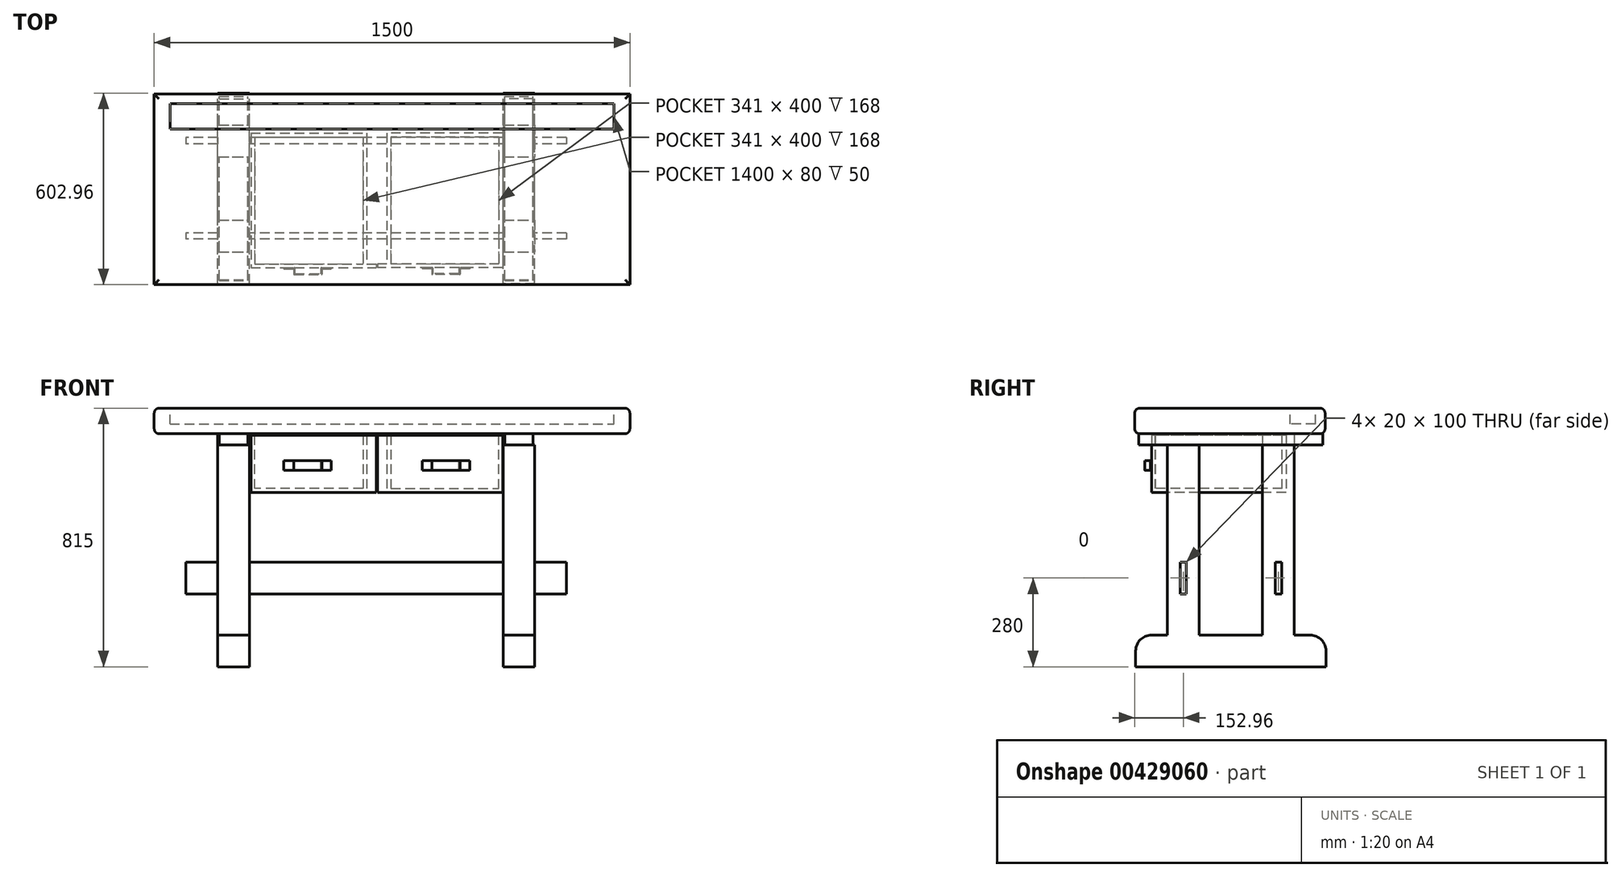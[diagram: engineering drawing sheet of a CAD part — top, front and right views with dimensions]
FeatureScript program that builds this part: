
annotation { "Feature Type Name" : "Feature", "Feature Type Description" : "" }
export const myFeature = defineFeature(function(context is Context, id is Id, definition is map)
    precondition{}
    {
        {
            var Q0;
            Q0=qCreatedBy(makeId("Top.planeOp"),FACE);
            var sketch = newSketch(context, id + "F0", { "sketchPlane" : qUnion([Q0])});
            skLineSegment(sketch, "E0.bottom", {"start": v(0, 0) * mm, "end": v(100, 0) * mm});
            skLineSegment(sketch, "E0.top", {"start": v(0, 600) * mm, "end": v(100, 600) * mm});
            skLineSegment(sketch, "E0.left", {"start": v(0, 0) * mm, "end": v(0, 600) * mm});
            skLineSegment(sketch, "E0.right", {"start": v(100, 0) * mm, "end": v(100, 600) * mm});
            skLineSegment(sketch, "E1.bottom", {"start": v(1000, 0) * mm, "end": v(900, 0) * mm});
            skLineSegment(sketch, "E1.top", {"start": v(1000, 600) * mm, "end": v(900, 600) * mm});
            skLineSegment(sketch, "E1.left", {"start": v(1000, 0) * mm, "end": v(1000, 600) * mm});
            skLineSegment(sketch, "E1.right", {"start": v(900, 0) * mm, "end": v(900, 600) * mm});
            skSolve(sketch);
        }
        {
            var Q0;
            Q0=makeQuery(id+"F0.imprint","IMPRINT",FACE,{"disambiguationData":[TD([[makeQuery(id+"F0.imprint","IMPRINT",EDGE,{"derivedFrom":sQuery(id+"F0.wireOp",EDGE,"E0.bottom")}),1.0]])]});
            var Q1;
            Q1=makeQuery(id+"F0.imprint","IMPRINT",FACE,{"disambiguationData":[TD([[makeQuery(id+"F0.imprint","IMPRINT",EDGE,{"derivedFrom":sQuery(id+"F0.wireOp",EDGE,"E1.bottom")}),-1.0]])]});
            extrude(context, id + "F1", {"entities" : qUnion([Q0, Q1]), "depth" : 100 * mm});
        }
        {
            var Q0;
            Q0=makeQuery(id+"F1.opExtrude","CAP_FACE",FACE,{"disambiguationData":[OSD([sQuery(id+"F0.wireOp",EDGE,"E0.bottom"),sQuery(id+"F0.wireOp",EDGE,"E0.top"),sQuery(id+"F0.wireOp",EDGE,"E0.left"),sQuery(id+"F0.wireOp",EDGE,"E0.right")])],"isStart":false});
            var sketch = newSketch(context, id + "F2", { "sketchPlane" : qUnion([Q0])});
            skLineSegment(sketch, "E2.bottom", {"start": v(0, 500) * mm, "end": v(100, 500) * mm});
            skLineSegment(sketch, "E2.top", {"start": v(0, 400) * mm, "end": v(100, 400) * mm});
            skLineSegment(sketch, "E2.left", {"start": v(0, 500) * mm, "end": v(0, 400) * mm});
            skLineSegment(sketch, "E2.right", {"start": v(100, 500) * mm, "end": v(100, 400) * mm});
            skLineSegment(sketch, "E3.bottom", {"start": v(0, 200) * mm, "end": v(100, 200) * mm});
            skLineSegment(sketch, "E3.top", {"start": v(0, 100) * mm, "end": v(100, 100) * mm});
            skLineSegment(sketch, "E3.left", {"start": v(0, 200) * mm, "end": v(0, 100) * mm});
            skLineSegment(sketch, "E3.right", {"start": v(100, 200) * mm, "end": v(100, 100) * mm});
            skLineSegment(sketch, "E4.1.0.0", {"start": v(900, 200) * mm, "end": v(900, 100) * mm});
            skLineSegment(sketch, "E4.1.0.1", {"start": v(1000, 200) * mm, "end": v(1000, 100) * mm});
            skLineSegment(sketch, "E4.1.0.2", {"start": v(900, 100) * mm, "end": v(1000, 100) * mm});
            skLineSegment(sketch, "E4.1.0.3", {"start": v(900, 200) * mm, "end": v(1000, 200) * mm});
            skLineSegment(sketch, "E4.1.0.4", {"start": v(1000, 500) * mm, "end": v(1000, 400) * mm});
            skLineSegment(sketch, "E4.1.0.5", {"start": v(900, 500) * mm, "end": v(900, 400) * mm});
            skLineSegment(sketch, "E4.1.0.6", {"start": v(900, 400) * mm, "end": v(1000, 400) * mm});
            skLineSegment(sketch, "E4.1.0.7", {"start": v(900, 500) * mm, "end": v(1000, 500) * mm});
            skLineSegment(sketch, "E4.direction1", {"start": v(0, 100) * mm, "end": v(900, 100) * mm, "construction": true});
            skSolve(sketch);
        }
        {
            var Q0;
            Q0=makeQuery(id+"F2.imprint","IMPRINT",FACE,{"disambiguationData":[TD([[makeQuery(id+"F2.imprint","IMPRINT",EDGE,{"derivedFrom":sQuery(id+"F2.wireOp",EDGE,"E2.bottom")}),-1.0]])]});
            var Q1;
            Q1=makeQuery(id+"F2.imprint","IMPRINT",FACE,{"disambiguationData":[TD([[makeQuery(id+"F2.imprint","IMPRINT",EDGE,{"derivedFrom":sQuery(id+"F2.wireOp",EDGE,"E4.1.0.4")}),-1.0]])]});
            var Q2;
            Q2=makeQuery(id+"F2.imprint","IMPRINT",FACE,{"disambiguationData":[TD([[makeQuery(id+"F2.imprint","IMPRINT",EDGE,{"derivedFrom":sQuery(id+"F2.wireOp",EDGE,"E4.1.0.0")}),1.0]])]});
            var Q3;
            Q3=makeQuery(id+"F2.imprint","IMPRINT",FACE,{"disambiguationData":[TD([[makeQuery(id+"F2.imprint","IMPRINT",EDGE,{"derivedFrom":sQuery(id+"F2.wireOp",EDGE,"E3.bottom")}),-1.0]])]});
            extrude(context, id + "F3", {"entities" : qUnion([Q0, Q1, Q2, Q3]), "depth" : 600 * mm});
        }
        {
            var Q0;
            Q0=qCreatedBy(makeId("Right.planeOp"),FACE);
            cPlane(context, id + "F4", {"entities" : qUnion([Q0]), "cplaneType" : CPlaneType.OFFSET, "offset" : 100 * mm, "oppositeDirection" : true, "width" : 150 * mm, "height" : 150 * mm});
        }
        {
            var Q0;
            Q0=qCreatedBy(id+"F4.planeOp",FACE);
            var sketch = newSketch(context, id + "F5", { "sketchPlane" : qUnion([Q0])});
            skLineSegment(sketch, "E5.bottom", {"start": v(160, 330) * mm, "end": v(140, 330) * mm});
            skLineSegment(sketch, "E5.top", {"start": v(160, 230) * mm, "end": v(140, 230) * mm});
            skLineSegment(sketch, "E5.left", {"start": v(160, 330) * mm, "end": v(160, 230) * mm});
            skLineSegment(sketch, "E5.right", {"start": v(140, 330) * mm, "end": v(140, 230) * mm});
            skLineSegment(sketch, "E6.1.0.0", {"start": v(460, 330) * mm, "end": v(440, 330) * mm});
            skLineSegment(sketch, "E6.1.0.1", {"start": v(460, 230) * mm, "end": v(440, 230) * mm});
            skLineSegment(sketch, "E6.1.0.2", {"start": v(460, 330) * mm, "end": v(460, 230) * mm});
            skLineSegment(sketch, "E6.1.0.3", {"start": v(440, 330) * mm, "end": v(440, 230) * mm});
            skLineSegment(sketch, "E6.direction1", {"start": v(140, 230) * mm, "end": v(440, 230) * mm, "construction": true});
            skSolve(sketch);
        }
        {
            var Q0;
            Q0=makeQuery(id+"F5.imprint","IMPRINT",FACE,{"disambiguationData":[TD([[makeQuery(id+"F5.imprint","IMPRINT",EDGE,{"derivedFrom":sQuery(id+"F5.wireOp",EDGE,"E6.1.0.0")}),1.0]])]});
            var Q1;
            Q1=makeQuery(id+"F5.imprint","IMPRINT",FACE,{"disambiguationData":[TD([[makeQuery(id+"F5.imprint","IMPRINT",EDGE,{"derivedFrom":sQuery(id+"F5.wireOp",EDGE,"E5.bottom")}),1.0]])]});
            extrude(context, id + "F6", {"entities" : qUnion([Q0, Q1]), "depth" : 1200 * mm});
        }
        {
            var Q0;
            Q0=makeQuery(id+"F1.opExtrude","CAP_EDGE",EDGE,{"disambiguationData":[OSD([sQuery(id+"F0.wireOp",EDGE,"E0.top")])],"isStart":false});
            var Q1;
            Q1=makeQuery(id+"F1.opExtrude","CAP_EDGE",EDGE,{"disambiguationData":[OSD([sQuery(id+"F0.wireOp",EDGE,"E0.bottom")])],"isStart":false});
            var Q2;
            Q2=makeQuery(id+"F1.opExtrude","CAP_EDGE",EDGE,{"disambiguationData":[OSD([sQuery(id+"F0.wireOp",EDGE,"E1.bottom")])],"isStart":false});
            var Q3;
            Q3=makeQuery(id+"F1.opExtrude","CAP_EDGE",EDGE,{"disambiguationData":[OSD([sQuery(id+"F0.wireOp",EDGE,"E1.top")])],"isStart":false});
            fillet(context, id + "F7", {"entities" : qUnion([Q0, Q1, Q2, Q3]), "radius" : 50 * mm, "tangentPropagation" : true, "allowEdgeOverflow" : false});
        }
        {
            var Q0;
            Q0=makeQuery(id+"F3.opExtrude","CAP_FACE",FACE,{"disambiguationData":[OSD([sQuery(id+"F2.wireOp",EDGE,"E2.bottom"),sQuery(id+"F2.wireOp",EDGE,"E2.top"),sQuery(id+"F2.wireOp",EDGE,"E2.left"),sQuery(id+"F2.wireOp",EDGE,"E2.right")])],"isStart":false});
            var sketch = newSketch(context, id + "F8", { "sketchPlane" : qUnion([Q0])});
            skLineSegment(sketch, "E7.bottom", {"start": v(5, 10) * mm, "end": v(95, 10) * mm});
            skLineSegment(sketch, "E7.top", {"start": v(5, 590) * mm, "end": v(95, 590) * mm});
            skLineSegment(sketch, "E7.left", {"start": v(5, 10) * mm, "end": v(5, 590) * mm});
            skLineSegment(sketch, "E7.right", {"start": v(95, 10) * mm, "end": v(95, 590) * mm});
            skLineSegment(sketch, "E8.1.0.0", {"start": v(995, 10) * mm, "end": v(995, 590) * mm});
            skLineSegment(sketch, "E8.1.0.1", {"start": v(905, 10) * mm, "end": v(905, 590) * mm});
            skLineSegment(sketch, "E8.1.0.2", {"start": v(905, 590) * mm, "end": v(995, 590) * mm});
            skLineSegment(sketch, "E8.1.0.3", {"start": v(905, 10) * mm, "end": v(995, 10) * mm});
            skSolve(sketch);
        }
        {
            var Q0;
            Q0=makeQuery(id+"F8.imprint","IMPRINT",FACE,{"disambiguationData":[TD([[makeQuery(id+"F8.imprint","IMPRINT",EDGE,{"derivedFrom":sQuery(id+"F8.wireOp",EDGE,"E8.1.0.0")}),1.0]])]});
            var Q1;
            {var subQ0=sQuery(id+"F8.wireOp",EDGE,"E7.top");Q1=makeQuery(id+"F8.imprint","IMPRINT",FACE,{"disambiguationData":[TD([[makeQuery(id+"F8.imprint","IMPRINT",EDGE,{"derivedFrom":subQ0}),-1.0]])]});}
            var Q2;
            {var subQ1=makeQuery(id+"F3.opExtrude","CAP_EDGE",EDGE,{"disambiguationData":[OSD([sQuery(id+"F2.wireOp",EDGE,"E2.bottom")])],"isStart":false});Q2=makeQuery(id+"F8.imprint","IMPRINT",FACE,{"disambiguationData":[TD([[makeQuery(id+"F8.imprint","IMPRINT",EDGE,{"derivedFrom":subQ1}),-1.0]])]});}
            var Q3;
            {var subQ0=sQuery(id+"F8.wireOp",EDGE,"E7.bottom");Q3=makeQuery(id+"F8.imprint","IMPRINT",FACE,{"disambiguationData":[TD([[makeQuery(id+"F8.imprint","IMPRINT",EDGE,{"derivedFrom":subQ0}),1.0]])]});}
            extrude(context, id + "F9", {"entities" : qUnion([Q0, Q1, Q2, Q3]), "depth" : 35 * mm});
        }
        {
            var Q0;
            Q0=makeQuery(id+"F9.opExtrude","CAP_FACE",FACE,{"disambiguationData":[OSD([sQuery(id+"F8.wireOp",EDGE,"E8.1.0.0"),sQuery(id+"F8.wireOp",EDGE,"E8.1.0.1"),sQuery(id+"F8.wireOp",EDGE,"E8.1.0.2"),sQuery(id+"F8.wireOp",EDGE,"E8.1.0.3")])],"isStart":false});
            var sketch = newSketch(context, id + "F10", { "sketchPlane" : qUnion([Q0])});
            skLineSegment(sketch, "E9.bottom", {"start": v(-200, 597.04) * mm, "end": v(1300, 597.04) * mm});
            skLineSegment(sketch, "E9.top", {"start": v(-200, -2.96) * mm, "end": v(1300, -2.96) * mm});
            skLineSegment(sketch, "E9.left", {"start": v(-200, 597.04) * mm, "end": v(-200, -2.96) * mm});
            skLineSegment(sketch, "E9.right", {"start": v(1300, 597.04) * mm, "end": v(1300, -2.96) * mm});
            skSolve(sketch);
        }
        {
            var Q0;
            Q0=makeQuery(id+"F10.imprint","IMPRINT",FACE,{"disambiguationData":[TD([[makeQuery(id+"F10.imprint","IMPRINT",EDGE,{"derivedFrom":sQuery(id+"F10.wireOp",EDGE,"E9.top")}),1.0]])]});
            var Q1;
            {var subQ5=makeQuery(id+"F9.opExtrude","CAP_EDGE",EDGE,{"disambiguationData":[OSD([sQuery(id+"F8.wireOp",EDGE,"E8.1.0.3")])],"isStart":false});Q1=makeQuery(id+"F10.imprint","IMPRINT",FACE,{"disambiguationData":[TD([[makeQuery(id+"F10.imprint","IMPRINT",EDGE,{"derivedFrom":subQ5}),1.0]])]});}
            extrude(context, id + "F11", {"entities" : qUnion([Q0, Q1]), "depth" : 80 * mm});
        }
        {
            var Q0;
            Q0=makeQuery(id+"F11.opExtrude","CAP_FACE",FACE,{"disambiguationData":[OSD([sQuery(id+"F10.wireOp",EDGE,"E9.bottom"),sQuery(id+"F10.wireOp",EDGE,"E9.top"),sQuery(id+"F10.wireOp",EDGE,"E9.left"),sQuery(id+"F10.wireOp",EDGE,"E9.right")])],"isStart":false});
            var Q1;
            Q1=makeQuery(id+"F11.opExtrude","CAP_FACE",FACE,{"disambiguationData":[OSD([sQuery(id+"F10.wireOp",EDGE,"E9.bottom"),sQuery(id+"F10.wireOp",EDGE,"E9.top"),sQuery(id+"F10.wireOp",EDGE,"E9.left"),sQuery(id+"F10.wireOp",EDGE,"E9.right")])],"isStart":true});
            fillet(context, id + "F12", {"entities" : qUnion([Q0, Q1]), "radius" : 15 * mm, "tangentPropagation" : true, "allowEdgeOverflow" : false});
        }
        {
            var Q0;
            Q0=makeQuery(id+"F1.opExtrude","SWEPT_BODY",BODY,{"disambiguationData":[OSD([sQuery(id+"F0.wireOp",EDGE,"E0.bottom"),sQuery(id+"F0.wireOp",EDGE,"E0.top"),sQuery(id+"F0.wireOp",EDGE,"E0.left"),sQuery(id+"F0.wireOp",EDGE,"E0.right")])]});
            var Q1;
            Q1=makeQuery(id+"F1.opExtrude","SWEPT_BODY",BODY,{"disambiguationData":[OSD([sQuery(id+"F0.wireOp",EDGE,"E1.bottom"),sQuery(id+"F0.wireOp",EDGE,"E1.top"),sQuery(id+"F0.wireOp",EDGE,"E1.left"),sQuery(id+"F0.wireOp",EDGE,"E1.right")])]});
            var Q2;
            Q2=makeQuery(id+"F3.opExtrude","SWEPT_BODY",BODY,{"disambiguationData":[OSD([sQuery(id+"F2.wireOp",EDGE,"E2.bottom"),sQuery(id+"F2.wireOp",EDGE,"E2.top"),sQuery(id+"F2.wireOp",EDGE,"E2.left"),sQuery(id+"F2.wireOp",EDGE,"E2.right")])]});
            var Q3;
            Q3=makeQuery(id+"F3.opExtrude","SWEPT_BODY",BODY,{"disambiguationData":[OSD([sQuery(id+"F2.wireOp",EDGE,"E3.bottom"),sQuery(id+"F2.wireOp",EDGE,"E3.top"),sQuery(id+"F2.wireOp",EDGE,"E3.left"),sQuery(id+"F2.wireOp",EDGE,"E3.right")])]});
            var Q4;
            Q4=makeQuery(id+"F3.opExtrude","SWEPT_BODY",BODY,{"disambiguationData":[OSD([sQuery(id+"F2.wireOp",EDGE,"E4.1.0.0"),sQuery(id+"F2.wireOp",EDGE,"E4.1.0.1"),sQuery(id+"F2.wireOp",EDGE,"E4.1.0.2"),sQuery(id+"F2.wireOp",EDGE,"E4.1.0.3")])]});
            var Q5;
            Q5=makeQuery(id+"F3.opExtrude","SWEPT_BODY",BODY,{"disambiguationData":[OSD([sQuery(id+"F2.wireOp",EDGE,"E4.1.0.4"),sQuery(id+"F2.wireOp",EDGE,"E4.1.0.5"),sQuery(id+"F2.wireOp",EDGE,"E4.1.0.6"),sQuery(id+"F2.wireOp",EDGE,"E4.1.0.7")])]});
            var Q6;
            Q6=makeQuery(id+"F6.opExtrude","SWEPT_BODY",BODY,{"disambiguationData":[OSD([sQuery(id+"F5.wireOp",EDGE,"E5.bottom"),sQuery(id+"F5.wireOp",EDGE,"E5.top"),sQuery(id+"F5.wireOp",EDGE,"E5.left"),sQuery(id+"F5.wireOp",EDGE,"E5.right")])]});
            var Q7;
            Q7=makeQuery(id+"F6.opExtrude","SWEPT_BODY",BODY,{"disambiguationData":[OSD([sQuery(id+"F5.wireOp",EDGE,"E6.1.0.0"),sQuery(id+"F5.wireOp",EDGE,"E6.1.0.1"),sQuery(id+"F5.wireOp",EDGE,"E6.1.0.2"),sQuery(id+"F5.wireOp",EDGE,"E6.1.0.3")])]});
            var Q8;
            Q8=makeQuery(id+"F9.opExtrude","SWEPT_BODY",BODY,{"disambiguationData":[OSD([sQuery(id+"F8.wireOp",EDGE,"E7.bottom"),sQuery(id+"F8.wireOp",EDGE,"E7.top"),sQuery(id+"F8.wireOp",EDGE,"E7.left"),sQuery(id+"F8.wireOp",EDGE,"E7.right")])]});
            var Q9;
            Q9=makeQuery(id+"F9.opExtrude","SWEPT_BODY",BODY,{"disambiguationData":[OSD([sQuery(id+"F8.wireOp",EDGE,"E8.1.0.0"),sQuery(id+"F8.wireOp",EDGE,"E8.1.0.1"),sQuery(id+"F8.wireOp",EDGE,"E8.1.0.2"),sQuery(id+"F8.wireOp",EDGE,"E8.1.0.3")])]});
            var Q10;
            Q10=makeQuery(id+"F11.opExtrude","SWEPT_BODY",BODY,{"disambiguationData":[OSD([sQuery(id+"F10.wireOp",EDGE,"E9.bottom"),sQuery(id+"F10.wireOp",EDGE,"E9.top"),sQuery(id+"F10.wireOp",EDGE,"E9.left"),sQuery(id+"F10.wireOp",EDGE,"E9.right")])]});
            booleanBodies(context, id + "F13", {"operationType" : BooleanOperationType.UNION, "tools" : qUnion([Q0, Q1, Q2, Q3, Q4, Q5, Q6, Q7, Q8, Q9, Q10])});
        }
        {
            var Q0;
            Q0=makeQuery(id+"F11.opExtrude","CAP_FACE",FACE,{"disambiguationData":[OSD([sQuery(id+"F10.wireOp",EDGE,"E9.bottom"),sQuery(id+"F10.wireOp",EDGE,"E9.top"),sQuery(id+"F10.wireOp",EDGE,"E9.left"),sQuery(id+"F10.wireOp",EDGE,"E9.right")])],"isStart":false});
            var sketch = newSketch(context, id + "F14", { "sketchPlane" : qUnion([Q0])});
            skLineSegment(sketch, "E10.bottom", {"start": v(-150, 567.04) * mm, "end": v(1250, 567.04) * mm});
            skLineSegment(sketch, "E10.top", {"start": v(-150, 487.04) * mm, "end": v(1250, 487.04) * mm});
            skLineSegment(sketch, "E10.left", {"start": v(-150, 567.04) * mm, "end": v(-150, 487.04) * mm});
            skLineSegment(sketch, "E10.right", {"start": v(1250, 567.04) * mm, "end": v(1250, 487.04) * mm});
            skSolve(sketch);
        }
        {
            var Q0;
            Q0=makeQuery(id+"F14.imprint","IMPRINT",FACE,{"disambiguationData":[TD([[makeQuery(id+"F14.imprint","IMPRINT",EDGE,{"derivedFrom":sQuery(id+"F14.wireOp",EDGE,"E10.bottom")}),-1.0]])]});
            extrude(context, id + "F15", {"entities" : qUnion([Q0]), "operationType" : NewBodyOperationType.REMOVE, "oppositeDirection" : true, "depth" : 50 * mm});
        }
        {
            var Q0;
            Q0=qCreatedBy(makeId("Front.planeOp"),FACE);
            cPlane(context, id + "F16", {"entities" : qUnion([Q0]), "cplaneType" : CPlaneType.OFFSET, "offset" : 50 * mm, "oppositeDirection" : true, "width" : 150 * mm, "height" : 150 * mm});
        }
        {
            var Q0;
            Q0=qCreatedBy(id+"F16.planeOp",FACE);
            var sketch = newSketch(context, id + "F17", { "sketchPlane" : qUnion([Q0])});
            skLineSegment(sketch, "E11.bottom", {"start": v(105, 730) * mm, "end": v(500, 730) * mm});
            skLineSegment(sketch, "E11.top", {"start": v(105, 550) * mm, "end": v(500, 550) * mm});
            skLineSegment(sketch, "E11.left", {"start": v(105, 730) * mm, "end": v(105, 550) * mm});
            skLineSegment(sketch, "E11.right", {"start": v(500, 730) * mm, "end": v(500, 550) * mm});
            skLineSegment(sketch, "E12", {"start": v(105, 730) * mm, "end": v(900, 730) * mm, "construction": true});
            skPoint(sketch, "E12.startSnap0", {"position": v(105, 640) * mm});
            skLineSegment(sketch, "E13", {"start": v(502.5, 730) * mm, "end": v(502.5, 502.03) * mm, "construction": true});
            skSolve(sketch);
        }
        {
            var Q0;
            Q0=makeQuery(id+"F17.imprint","IMPRINT",FACE,{"disambiguationData":[TD([[makeQuery(id+"F17.imprint","IMPRINT",EDGE,{"derivedFrom":sQuery(id+"F17.wireOp",EDGE,"E11.bottom")}),-1.0]])]});
            extrude(context, id + "F18", {"entities" : qUnion([Q0]), "oppositeDirection" : true, "depth" : 12 * mm});
        }
        {
            var Q0;
            Q0=makeQuery(id+"F18.opExtrude","CAP_FACE",FACE,{"disambiguationData":[OSD([sQuery(id+"F17.wireOp",EDGE,"E11.bottom"),sQuery(id+"F17.wireOp",EDGE,"E11.top"),sQuery(id+"F17.wireOp",EDGE,"E11.left"),sQuery(id+"F17.wireOp",EDGE,"E11.right")])],"isStart":false});
            var sketch = newSketch(context, id + "F19", { "sketchPlane" : qUnion([Q0])});
            skLineSegment(sketch, "E14.bottom", {"start": v(-470, 730) * mm, "end": v(-458, 730) * mm});
            skLineSegment(sketch, "E14.top", {"start": v(-470, 550) * mm, "end": v(-458, 550) * mm});
            skLineSegment(sketch, "E14.left", {"start": v(-470, 730) * mm, "end": v(-470, 550) * mm});
            skLineSegment(sketch, "E14.right", {"start": v(-458, 730) * mm, "end": v(-458, 562) * mm});
            skLineSegment(sketch, "E15.bottom", {"start": v(-470, 550) * mm, "end": v(-105, 550) * mm});
            skLineSegment(sketch, "E15.top", {"start": v(-458, 562) * mm, "end": v(-117, 562) * mm});
            skLineSegment(sketch, "E15.left", {"start": v(-470, 550) * mm, "end": v(-470, 562) * mm});
            skLineSegment(sketch, "E15.right", {"start": v(-105, 550) * mm, "end": v(-105, 562) * mm});
            skLineSegment(sketch, "E16.bottom", {"start": v(-105, 550) * mm, "end": v(-117, 550) * mm});
            skLineSegment(sketch, "E16.top", {"start": v(-105, 730) * mm, "end": v(-117, 730) * mm});
            skLineSegment(sketch, "E16.left", {"start": v(-105, 550) * mm, "end": v(-105, 730) * mm});
            skLineSegment(sketch, "E16.right", {"start": v(-117, 562) * mm, "end": v(-117, 730) * mm});
            skLineSegment(sketch, "E17", {"start": v(-287.5, 562) * mm, "end": v(-287.5, 550) * mm, "construction": true});
            skSolve(sketch);
        }
        {
            var Q0;
            Q0=makeQuery(id+"F19.imprint","IMPRINT",FACE,{"disambiguationData":[TD([[makeQuery(id+"F19.imprint","IMPRINT",EDGE,{"derivedFrom":sQuery(id+"F19.wireOp",EDGE,"E14.bottom")}),1.0]])]});
            extrude(context, id + "F20", {"entities" : qUnion([Q0]), "operationType" : NewBodyOperationType.ADD, "depth" : 400 * mm});
        }
        {
            var Q0;
            Q0=makeQuery(id+"F20.opExtrude","CAP_FACE",FACE,{"disambiguationData":[OSD([sQuery(id+"F19.wireOp",EDGE,"E14.bottom"),sQuery(id+"F19.wireOp",EDGE,"E14.left"),sQuery(id+"F19.wireOp",EDGE,"E14.right"),sQuery(id+"F19.wireOp",EDGE,"E15.bottom"),sQuery(id+"F19.wireOp",EDGE,"E15.top"),sQuery(id+"F19.wireOp",EDGE,"E15.left"),sQuery(id+"F19.wireOp",EDGE,"E16.bottom"),sQuery(id+"F19.wireOp",EDGE,"E16.top"),sQuery(id+"F19.wireOp",EDGE,"E16.left"),sQuery(id+"F19.wireOp",EDGE,"E16.right")])],"isStart":false});
            var sketch = newSketch(context, id + "F21", { "sketchPlane" : qUnion([Q0])});
            skLineSegment(sketch, "E18.bottom", {"start": v(-470, 730) * mm, "end": v(-105, 730) * mm});
            skLineSegment(sketch, "E18.top", {"start": v(-470, 550) * mm, "end": v(-105, 550) * mm});
            skLineSegment(sketch, "E18.left", {"start": v(-470, 730) * mm, "end": v(-470, 550) * mm});
            skLineSegment(sketch, "E18.right", {"start": v(-105, 730) * mm, "end": v(-105, 550) * mm});
            skSolve(sketch);
        }
        {
            var Q0;
            Q0=makeQuery(id+"F21.imprint","IMPRINT",FACE,{"disambiguationData":[TD([[makeQuery(id+"F21.imprint","IMPRINT",EDGE,{"derivedFrom":sQuery(id+"F21.wireOp",EDGE,"E18.top")}),-1.0]])]});
            var Q1;
            {var subQ1=makeQuery(id+"F20.opExtrude","CAP_EDGE",EDGE,{"disambiguationData":[OSD([sQuery(id+"F19.wireOp",EDGE,"E14.right")])],"isStart":false});Q1=makeQuery(id+"F21.imprint","IMPRINT",FACE,{"disambiguationData":[TD([[makeQuery(id+"F21.imprint","IMPRINT",EDGE,{"derivedFrom":subQ1}),1.0]])]});}
            extrude(context, id + "F22", {"entities" : qUnion([Q0, Q1]), "operationType" : NewBodyOperationType.ADD, "depth" : 12 * mm});
        }
        {
            var Q0;
            Q0=qCreatedBy(makeId("Top.planeOp"),FACE);
            cPlane(context, id + "F23", {"entities" : qUnion([Q0]), "cplaneType" : CPlaneType.OFFSET, "offset" : 650 * mm, "width" : 150 * mm, "height" : 150 * mm});
        }
        {
            var Q0;
            Q0=qCreatedBy(id+"F23.planeOp",FACE);
            var sketch = newSketch(context, id + "F24", { "sketchPlane" : qUnion([Q0])});
            skLineSegment(sketch, "E19.bottom", {"start": v(208.7, 50) * mm, "end": v(241.2, 50) * mm});
            skLineSegment(sketch, "E19.top", {"start": v(208.7, 47) * mm, "end": v(238.7, 47) * mm});
            skLineSegment(sketch, "E19.left", {"start": v(208.7, 50) * mm, "end": v(208.7, 47) * mm});
            skLineSegment(sketch, "E19.right", {"start": v(358.7, 50) * mm, "end": v(358.7, 47) * mm});
            skLineSegment(sketch, "E20.top", {"start": v(241.2, 28.45) * mm, "end": v(242.7, 28.45) * mm});
            skLineSegment(sketch, "E20.left", {"start": v(239.7, 46) * mm, "end": v(239.7, 29.95) * mm});
            skLineSegment(sketch, "E20.right", {"start": v(242.7, 48.5) * mm, "end": v(242.7, 32.45) * mm});
            skLineSegment(sketch, "E21.bottom", {"start": v(327.2, 50) * mm, "end": v(328.2, 50) * mm});
            skLineSegment(sketch, "E21.top", {"start": v(325.7, 28.45) * mm, "end": v(327.2, 28.45) * mm});
            skLineSegment(sketch, "E21.left", {"start": v(325.7, 48.5) * mm, "end": v(325.7, 32.45) * mm});
            skLineSegment(sketch, "E21.right", {"start": v(328.7, 47) * mm, "end": v(328.7, 29.95) * mm});
            skLineSegment(sketch, "E22", {"start": v(242.7, 28.45) * mm, "end": v(325.7, 28.45) * mm});
            skLineSegment(sketch, "E23", {"start": v(243.7, 31.45) * mm, "end": v(324.7, 31.45) * mm});
            skLineSegment(sketch, "E24.trimOffspring", {"start": v(325.7, 50) * mm, "end": v(358.7, 50) * mm});
            skLineSegment(sketch, "E25.trimOffspring", {"start": v(328.7, 47) * mm, "end": v(358.7, 47) * mm});
            skPoint(sketch, "E26.visualSharp", {"position": v(239.7, 47) * mm});
            skArc(sketch, "E26.filletArc", {"start": v(239.7, 46) * mm, "mid": v(239.41, 46.7) * mm, "end": v(238.7, 47) * mm});
            skPoint(sketch, "E27.visualSharp", {"position": v(239.7, 28.45) * mm});
            skArc(sketch, "E27.filletArc", {"start": v(239.7, 29.95) * mm, "mid": v(240.14, 28.9) * mm, "end": v(241.2, 28.45) * mm});
            skPoint(sketch, "E28.visualSharp", {"position": v(242.7, 31.45) * mm});
            skArc(sketch, "E28.filletArc", {"start": v(242.7, 32.45) * mm, "mid": v(243, 31.74) * mm, "end": v(243.7, 31.45) * mm});
            skPoint(sketch, "E29.visualSharp", {"position": v(325.7, 31.45) * mm});
            skArc(sketch, "E29.filletArc", {"start": v(324.7, 31.45) * mm, "mid": v(325.41, 31.74) * mm, "end": v(325.7, 32.45) * mm});
            skPoint(sketch, "E30.visualSharp", {"position": v(328.7, 28.45) * mm});
            skArc(sketch, "E30.filletArc", {"start": v(327.2, 28.45) * mm, "mid": v(328.26, 28.9) * mm, "end": v(328.7, 29.95) * mm});
            skPoint(sketch, "E31.visualSharp", {"position": v(242.7, 50) * mm});
            skArc(sketch, "E31.filletArc", {"start": v(242.7, 48.5) * mm, "mid": v(242.26, 49.56) * mm, "end": v(241.2, 50) * mm});
            skPoint(sketch, "E32.visualSharp", {"position": v(325.7, 50) * mm});
            skArc(sketch, "E32.filletArc", {"start": v(327.2, 50) * mm, "mid": v(326.14, 49.56) * mm, "end": v(325.7, 48.5) * mm});
            skLineSegment(sketch, "E33", {"start": v(105, 50) * mm, "end": v(500, 50) * mm});
            skLineSegment(sketch, "E34", {"start": v(284.2, 31.45) * mm, "end": v(284.2, 50) * mm, "construction": true});
            skPoint(sketch, "E34.endSnap0", {"position": v(224.95, 50) * mm});
            skSolve(sketch);
        }
        {
            var Q0;
            Q0=makeQuery(id+"F24.imprint","IMPRINT",FACE,{"disambiguationData":[TD([[makeQuery(id+"F24.imprint","IMPRINT",EDGE,{"derivedFrom":sQuery(id+"F24.wireOp",EDGE,"E19.top")}),1.0]])]});
            extrude(context, id + "F25", {"entities" : qUnion([Q0]), "operationType" : NewBodyOperationType.ADD, "oppositeDirection" : true, "depth" : 30 * mm});
        }
        {
            var Q0;
            Q0=makeQuery(id+"F18.opExtrude","SWEPT_FACE",FACE,{"disambiguationData":[OSD([sQuery(id+"F17.wireOp",EDGE,"E11.right")])]});
            cPlane(context, id + "F26", {"entities" : qUnion([Q0]), "cplaneType" : CPlaneType.OFFSET, "offset" : 2 * mm, "width" : 150 * mm, "height" : 150 * mm});
        }
        {
            var Q0;
            Q0=makeQuery(id+"F18.opExtrude","SWEPT_BODY",BODY,{"disambiguationData":[OSD([sQuery(id+"F17.wireOp",EDGE,"E11.bottom"),sQuery(id+"F17.wireOp",EDGE,"E11.top"),sQuery(id+"F17.wireOp",EDGE,"E11.left"),sQuery(id+"F17.wireOp",EDGE,"E11.right")])]});
            var Q1;
            Q1=qCreatedBy(id+"F26.planeOp",FACE);
            mirror(context, id + "F27", {"operationType" : NewBodyOperationType.ADD, "entities" : qUnion([Q0]), "mirrorPlane" : qUnion([Q1])});
        }
    });
